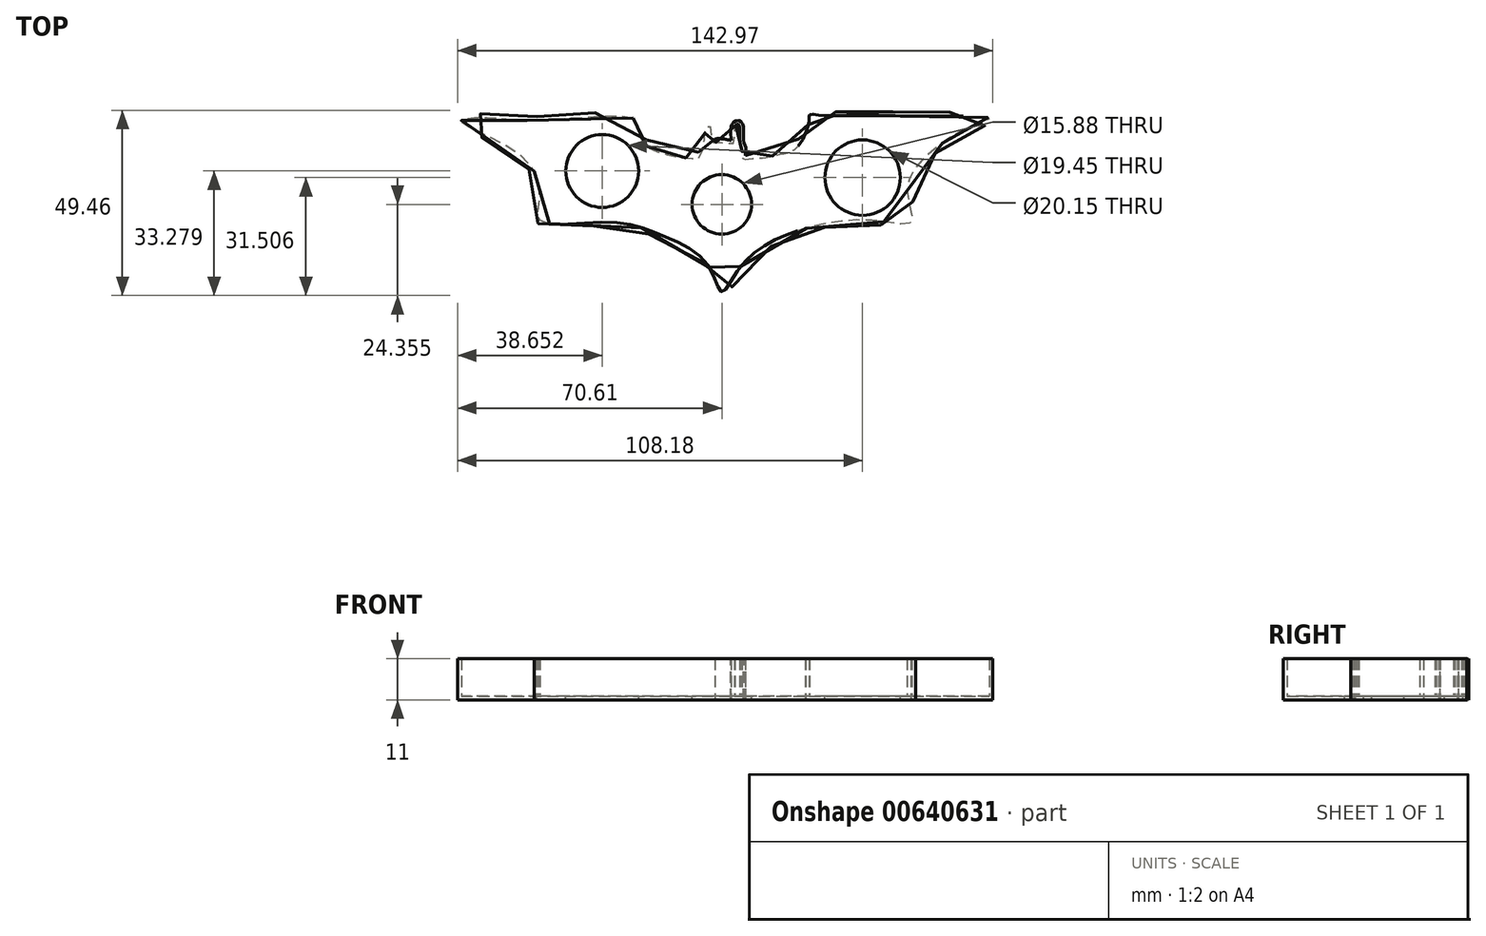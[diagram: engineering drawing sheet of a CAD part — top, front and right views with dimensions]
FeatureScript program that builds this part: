
annotation { "Feature Type Name" : "Feature", "Feature Type Description" : "" }
export const myFeature = defineFeature(function(context is Context, id is Id, definition is map)
    precondition{}
    {
        {
            var Q0;
            Q0=qCreatedBy(makeId("Top.planeOp"),FACE);
            var sketch = newSketch(context, id + "F0", { "sketchPlane" : qUnion([Q0])});
            skFitSpline(sketch, "E0", {"points": [v(-23.7, 17.98) * mm, v(-22.73, 15.97) * mm, v(-22.15, 13.5) * mm, v(-21.04, 11.75) * mm, v(-19.75, 10.13) * mm, v(-15.33, 8.44) * mm, v(-11.83, 7.6) * mm, v(-8.26, 7.2) * mm, v(-6.11, 7.34) * mm, v(-4.75, 11.62) * mm, v(-4.5, 14.67) * mm, v(-4.04, 15.97) * mm, v(-3.13, 15.71) * mm, v(-2.67, 11.75) * mm, v(-1.3, 11.5) * mm, v(1.35, 11.23) * mm, v(3.23, 11.36) * mm, v(3.43, 15.58) * mm, v(4.34, 16.36) * mm, v(4.8, 14.67) * mm, v(4.92, 11.17) * mm, v(5.38, 9.93) * mm, v(5.44, 7.34) * mm, v(7.95, 7.2) * mm, v(11.6, 7.48) * mm, v(15.68, 8.36) * mm, v(20.12, 10.18) * mm, v(23.26, 16.96) * mm, v(23.33, 18.12) * mm, v(23.48, 18.92) * mm, v(26.32, 18.7) * mm, v(32.36, 18.7) * mm, v(45.04, 18.63) * mm, v(52.04, 18.49) * mm, v(71.32, 17.9) * mm, v(65.93, 15.45) * mm, v(58.82, 11.29) * mm, v(52.45, 5.65) * mm, v(49.5, -1.95) * mm, v(50.49, -9.8) * mm, v(42.4, -9.55) * mm, v(28.43, -10.04) * mm, v(15.44, -13.96) * mm, v(4.9, -21.8) * mm, v(0, -28.42) * mm, v(-3.68, -21.31) * mm, v(-15.69, -13.47) * mm, v(-30.15, -9.8) * mm, v(-48.28, -9.55) * mm, v(-48.77, -4.64) * mm, v(-52.94, 7.36) * mm, v(-69.6, 17.17) * mm, v(-62.5, 18.15) * mm, v(-49.75, 17.41) * mm, v(-23.7, 17.98) * mm]});
            skSolve(sketch);
        }
        {
            var Q0;
            Q0=makeQuery(id+"F0.imprint","IMPRINT",FACE,{"disambiguationData":[TD([[makeQuery(id+"F0.imprint","IMPRINT",EDGE,{"derivedFrom":sQuery(id+"F0.wireOp",EDGE,"E0")}),-1.0]])]});
            extrude(context, id + "F1", {"entities" : qUnion([Q0]), "depth" : 10 * mm, "offsetDistance" : 25 * mm});
        }
        {
            var Q0;
            Q0=makeQuery(id+"F1.opExtrude","CAP_FACE",FACE,{"disambiguationData":[OSD([sQuery(id+"F0.wireOp",EDGE,"E0")])],"isStart":false});
            shell(context, id + "F2", {"entities" : qUnion([Q0]), "thickness" : 1 * mm, "oppositeDirection" : true});
        }
        {
            var Q0;
            Q0=makeQuery(id+"F0.imprint","IMPRINT",FACE,{"disambiguationData":[TD([[makeQuery(id+"F0.imprint","IMPRINT",EDGE,{"derivedFrom":sQuery(id+"F0.wireOp",EDGE,"E0")}),-1.0]])]});
            var sketch = newSketch(context, id + "F3", { "sketchPlane" : qUnion([Q0])});
            skCircle(sketch, "E1", {"center": v(0, -5.07) * mm, "radius": 7.94 * mm});
            skSolve(sketch);
        }
        {
            var Q0;
            Q0=makeQuery(id+"F3.imprint","IMPRINT",FACE,{"disambiguationData":[TD([[makeQuery(id+"F3.imprint","IMPRINT",EDGE,{"derivedFrom":sQuery(id+"F3.wireOp",EDGE,"E1")}),1.0]])]});
            extrude(context, id + "F4", {"entities" : qUnion([Q0]), "operationType" : NewBodyOperationType.REMOVE, "oppositeDirection" : true, "depth" : 25 * mm, "offsetDistance" : 25 * mm});
        }
        {
            var Q0;
            Q0=qCreatedBy(makeId("Top.planeOp"),FACE);
            var sketch = newSketch(context, id + "F5", { "sketchPlane" : qUnion([Q0])});
            skCircle(sketch, "E2", {"center": v(-31.96, 3.86) * mm, "radius": 9.72 * mm});
            skSolve(sketch);
        }
        {
            var Q0;
            Q0 = qSketchRegion(id + "F5", true);
            extrude(context, id + "F6", {"entities" : qUnion([Q0]), "operationType" : NewBodyOperationType.REMOVE, "oppositeDirection" : true, "depth" : 5 * mm, "offsetDistance" : 25 * mm});
        }
        {
            var Q0;
            Q0=qCreatedBy(makeId("Top.planeOp"),FACE);
            var sketch = newSketch(context, id + "F7", { "sketchPlane" : qUnion([Q0])});
            skCircle(sketch, "E3", {"center": v(37.57, 2.09) * mm, "radius": 10.08 * mm});
            skSolve(sketch);
        }
        {
            var Q0;
            Q0 = qSketchRegion(id + "F7", true);
            extrude(context, id + "F8", {"entities" : qUnion([Q0]), "operationType" : NewBodyOperationType.REMOVE, "oppositeDirection" : true, "depth" : 5 * mm, "offsetDistance" : 25 * mm});
        }
    });
